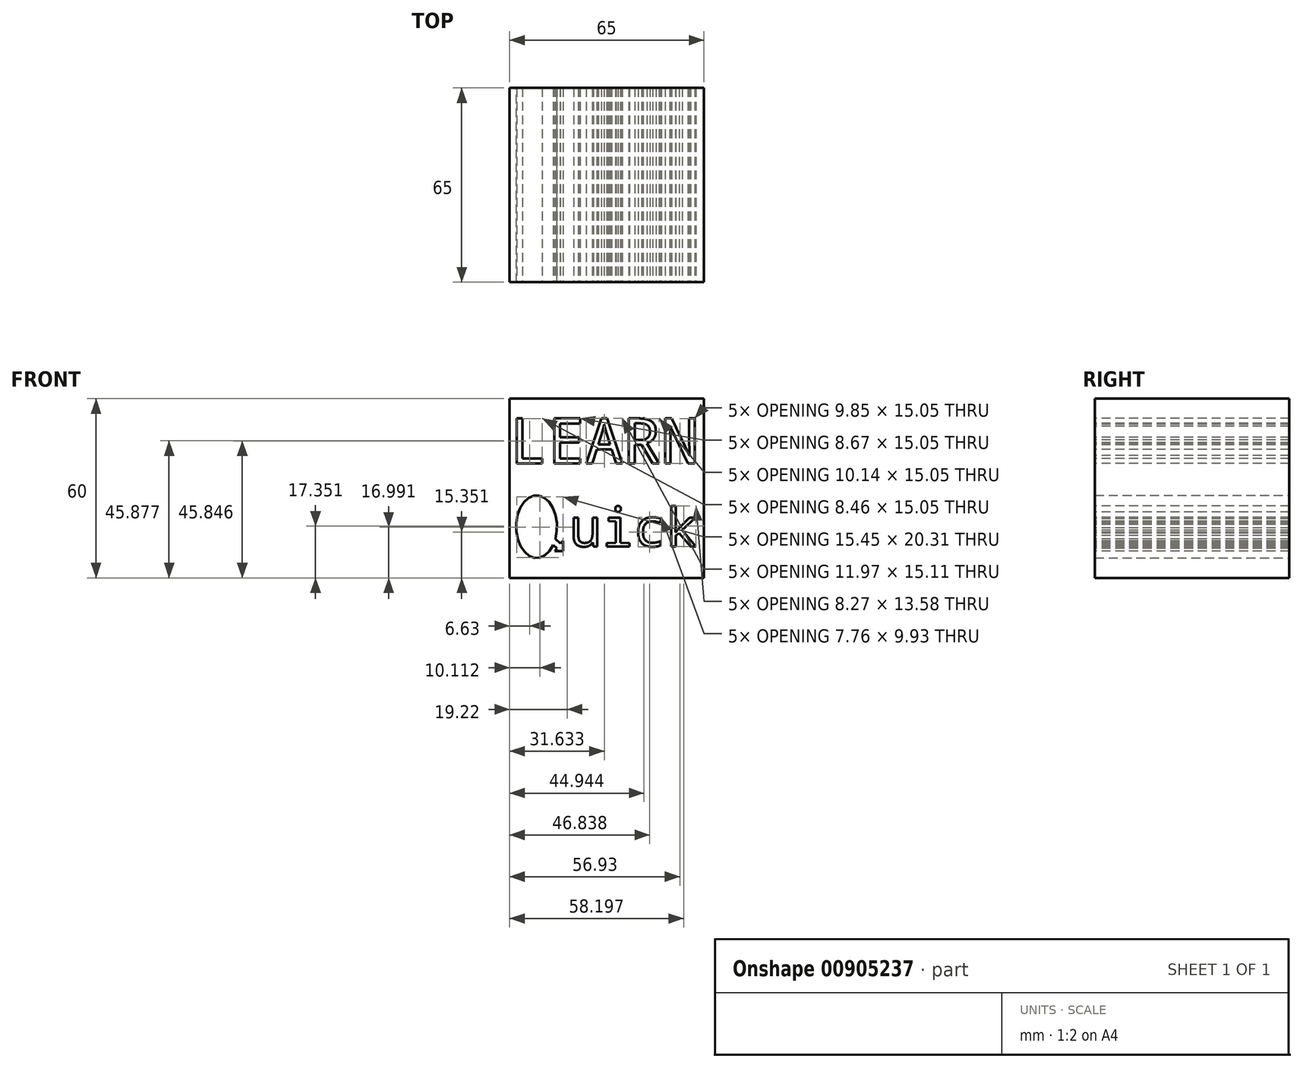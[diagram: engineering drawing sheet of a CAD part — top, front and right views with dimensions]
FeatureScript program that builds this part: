
annotation { "Feature Type Name" : "Feature", "Feature Type Description" : "" }
export const myFeature = defineFeature(function(context is Context, id is Id, definition is map)
    precondition{}
    {
        {
            var Q0;
            Q0=qCreatedBy(makeId("Top.planeOp"),FACE);
            var sketch = newSketch(context, id + "F0", { "sketchPlane" : qUnion([Q0])});
            skLineSegment(sketch, "E0.bottom", {"start": v(-32.5, 32.5) * mm, "end": v(32.5, 32.5) * mm});
            skLineSegment(sketch, "E0.top", {"start": v(-32.5, -32.5) * mm, "end": v(32.5, -32.5) * mm});
            skLineSegment(sketch, "E0.left", {"start": v(-32.5, 32.5) * mm, "end": v(-32.5, -32.5) * mm});
            skLineSegment(sketch, "E0.right", {"start": v(32.5, 32.5) * mm, "end": v(32.5, -32.5) * mm});
            skPoint(sketch, "E0.middle", {"position": v(0, 0) * mm});
            skSolve(sketch);
        }
        {
            var Q0;
            Q0=makeQuery(id+"F0.imprint","IMPRINT",FACE,{"disambiguationData":[TD([[makeQuery(id+"F0.imprint","IMPRINT",EDGE,{"derivedFrom":sQuery(id+"F0.wireOp",EDGE,"E0.bottom")}),-1.0]])]});
            extrude(context, id + "F1", {"entities" : qUnion([Q0]), "depth" : 60 * mm, "offsetDistance" : 25 * mm});
        }
        {
            var Q0;
            Q0=makeQuery(id+"F1.opExtrude","SWEPT_FACE",FACE,{"disambiguationData":[OSD([sQuery(id+"F0.wireOp",EDGE,"E0.top")])]});
            var sketch = newSketch(context, id + "F2", { "sketchPlane" : qUnion([Q0])});
            skText(sketch, "E1", { "text": "LEARN", "fontName": "DroidSansMono.ttf"});
            skText(sketch, "E2", { "text": "uick", "fontName": "DroidSansMono.ttf"});
            skPoint(sketch, "E3", {"position": v(-23.5, 17.13) * mm});
            skEllipse(sketch, "E4", {"center": v(-23.5, 17.13) * mm, "majorRadius": 10.48 * mm, "minorRadius": 6.82 * mm, "majorAxis": v(0, 1)});
            skLineSegment(sketch, "E5", {"start": v(-23.5, 17.13) * mm, "end": v(-22.85, 17.89) * mm});
            skLineSegment(sketch, "E6", {"start": v(-23.5, 17.13) * mm, "end": v(-24.15, 16.37) * mm});
            skLineSegment(sketch, "E7", {"start": v(-22.85, 17.89) * mm, "end": v(-15.48, 11.51) * mm});
            skLineSegment(sketch, "E8", {"start": v(-15.48, 11.51) * mm, "end": v(-14.66, 12.45) * mm});
            skLineSegment(sketch, "E9", {"start": v(-14.66, 12.45) * mm, "end": v(-14.66, 8.97) * mm});
            skLineSegment(sketch, "E10", {"start": v(-14.66, 8.97) * mm, "end": v(-17.5, 8.97) * mm});
            skLineSegment(sketch, "E11", {"start": v(-17.5, 8.97) * mm, "end": v(-16.68, 9.91) * mm});
            skLineSegment(sketch, "E12", {"start": v(-16.68, 9.91) * mm, "end": v(-24.15, 16.37) * mm});
            const initialGuessF2  = {"E1": [-0.0325, 0.03832, 1, 0, 0.01518], "E2": [-0.0125, 0.01056, 1, 0, 0.01287]};
            skSetInitialGuess(sketch, initialGuessF2);
            skSolve(sketch);
        }
        {
            var Q0;
            Q0 = qSketchRegion(id + "F2", true);
            extrude(context, id + "F3", {"entities" : qUnion([Q0]), "operationType" : NewBodyOperationType.REMOVE, "endBound" : BoundingType.THROUGH_ALL, "oppositeDirection" : true, "depth" : 25 * mm, "offsetDistance" : 25 * mm});
        }
    });
